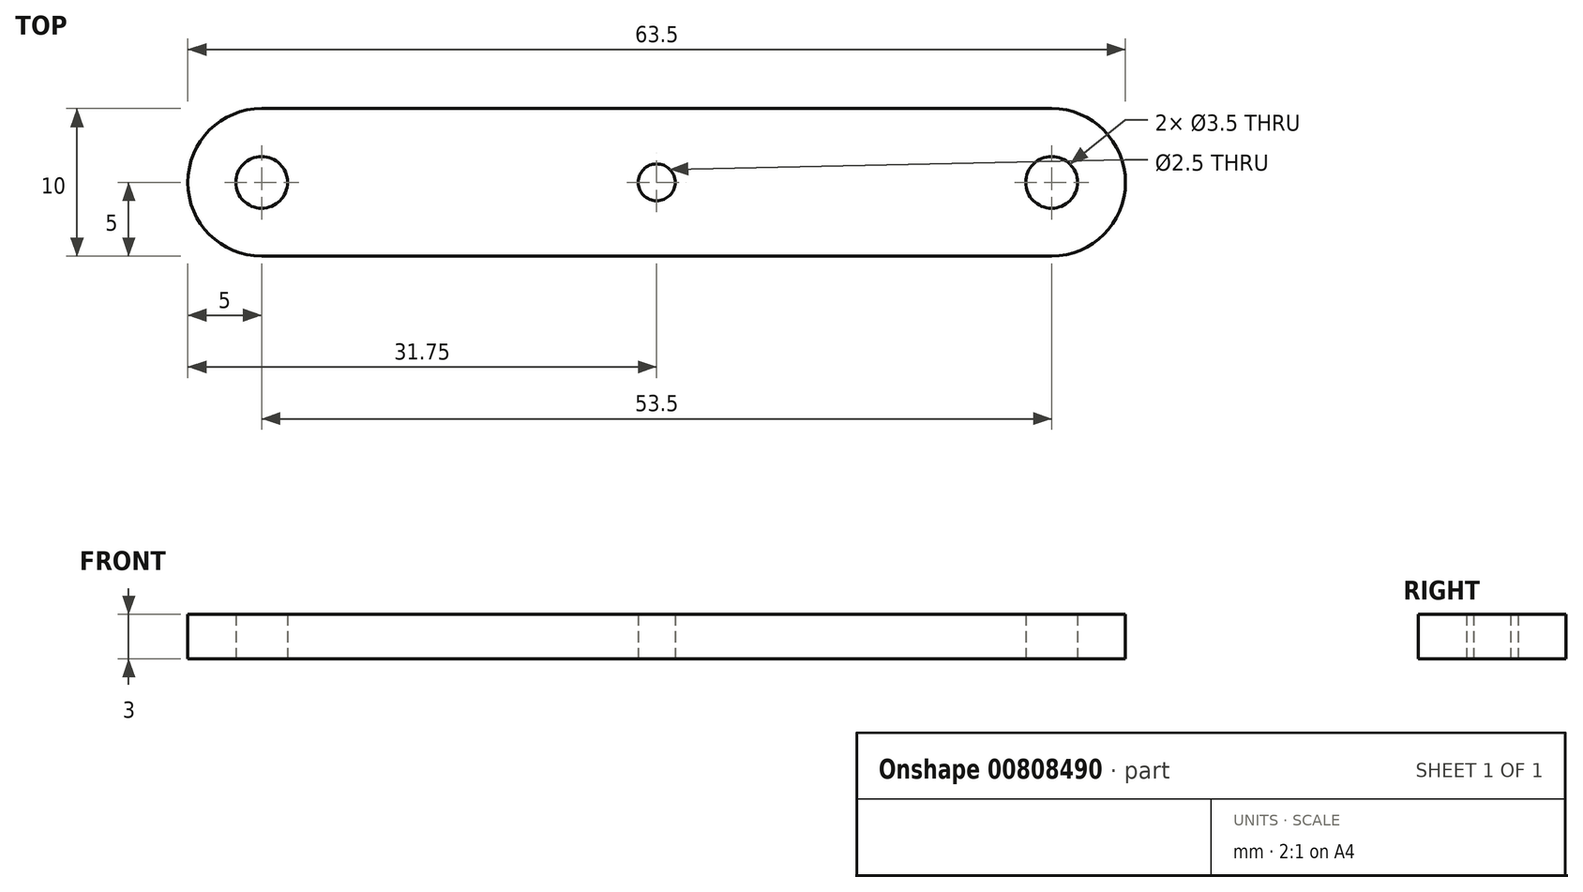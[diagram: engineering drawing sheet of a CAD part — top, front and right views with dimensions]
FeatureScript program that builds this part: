
annotation { "Feature Type Name" : "Feature", "Feature Type Description" : "" }
export const myFeature = defineFeature(function(context is Context, id is Id, definition is map)
    precondition{}
    {
        {
            var Q0;
            Q0=qCreatedBy(makeId("Top.planeOp"),FACE);
            var sketch = newSketch(context, id + "F0", { "sketchPlane" : qUnion([Q0])});
            skLineSegment(sketch, "E0", {"start": v(-26.75, 5) * mm, "end": v(26.75, 5) * mm});
            skLineSegment(sketch, "E1", {"start": v(-26.75, -5) * mm, "end": v(26.75, -5) * mm});
            skArc(sketch, "E2", {"start": v(-26.75, 5) * mm, "mid": v(-31.75, 0) * mm, "end": v(-26.75, -5) * mm});
            skArc(sketch, "E3", {"start": v(26.75, -5) * mm, "mid": v(31.75, 0) * mm, "end": v(26.75, 5) * mm});
            skCircle(sketch, "E4", {"center": v(-26.75, 0) * mm, "radius": 1.75 * mm});
            skCircle(sketch, "E5", {"center": v(26.75, 0) * mm, "radius": 1.75 * mm});
            skCircle(sketch, "E6", {"center": v(0, 0) * mm, "radius": 1.25 * mm});
            skLineSegment(sketch, "E7", {"start": v(0, 5) * mm, "end": v(0, -5) * mm, "construction": true});
            skSolve(sketch);
        }
        {
            var Q0;
            Q0 = qSketchRegion(id + "F0", true);
            extrude(context, id + "F1", {"entities" : qUnion([Q0]), "depth" : 3 * mm, "offsetDistance" : 25 * mm});
        }
    });
